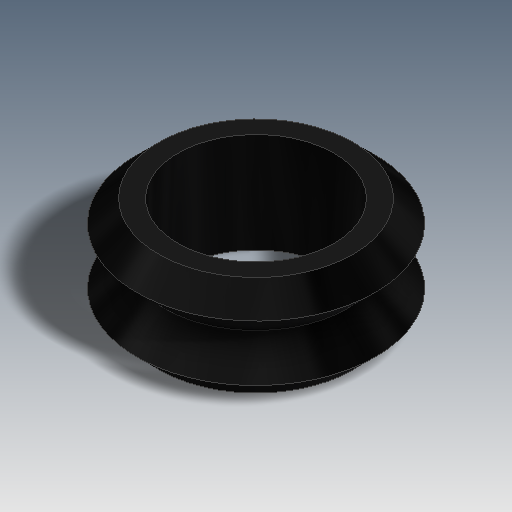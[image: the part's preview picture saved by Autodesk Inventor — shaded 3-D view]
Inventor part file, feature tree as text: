
AUTODESK INVENTOR PART (.ipt)
format: ipt  version: 2020 (Build 240168000, 168)  size: 139,776 bytes
history: native  units: in
note: dims shown in document units (in); Inventor stores cm internally (conversion verified against a paired STEP export)
features: revolve x1, sketch x1
ambient origin geometry x8: Origin, YZ Plane, XZ Plane, XY Plane, X Axis, Y Axis, Z Axis, Center Point
bodies: Solid1 (feature_tree)
feature tree (2):
  revolve  "Revolution1"  [1 undecoded]
  sketch  "Sketch1"  dims[d0=0.4028in d1=0.6289in d2=90.0deg d4=90.0deg d5=0.9602in d6=90.0deg]
note: 1 required parameter value undecoded (feature->parameter linkage not recoverable at this tier; creation-order binding heuristic only, values carry confidence <= 0.55)
